# Revit family: Gira_0268600
name_source: partatom
category: Electrical Fixtures
revit_build: Autodesk Revit 2017 (Build: 20160225_1515(x64)
units: mm (PartAtom-declared; Revit-internal decimal feet)

## family parameters
Cut with Voids When Loaded = No
Host = Face
Maintain Annotation Orientation = No
Part Type = Normal
Room Calculation Point = No
Round Connector Dimension = Use Diameter
Shared = No

## types (1)
- Blank cov.pl. sup.ring System 55 stainl.steel
    Assembly arrangement = Central cover plate
    Available = No
    BIM (1) = https://media.stage.bim.site und Tasten.rfa?public/gira/36a6b08/Sys55_Abdeckung_Schalten und Tasten.rfa
    Category = Insert/cover for communication technology
    Colour = Stainless steel
    Data sheet (1) = https://katalog.gira.de
    Default Elevation = 1219 mm
    Description = Bl.cov.pl.sup.r. Sys55 SST,Blank cover plate with support ring,,Stainless steel,Notes :,- For screw mounting only.
    GTIN = 4010337021865
    HAN = 0268600
    Halogen free = No
    HeinzeBIM = https://bimportal.heinze.de
    Imprintable label = Without indication field
    Luster terminal = No
    Manufacturer = Gira
    Manufacturer URL = https://www.gira.de
    Material = Metal
    Material quality = Stainless steel
    Mounting method = Flush mounted (plaster)
    Name = Blank cov.pl. sup.ring System 55 stainl.steel
    Suitable for degree of protection (IP) = IP20
    Support ring = Yes
    Surface finishing = Not applicable
    Surface protection = Other
    Transparent = No
    Type of fastening = Mounting with screw
    URL = http://katalog.gira.de
    Utilization = Blind cap
    With dust cover = No
    With hinged lid = No
    With imprint = No
    With strain relief = No

## geometry (parser evidence)
native form markers: Sweep x4
no freeform markers — native parametric forms only
